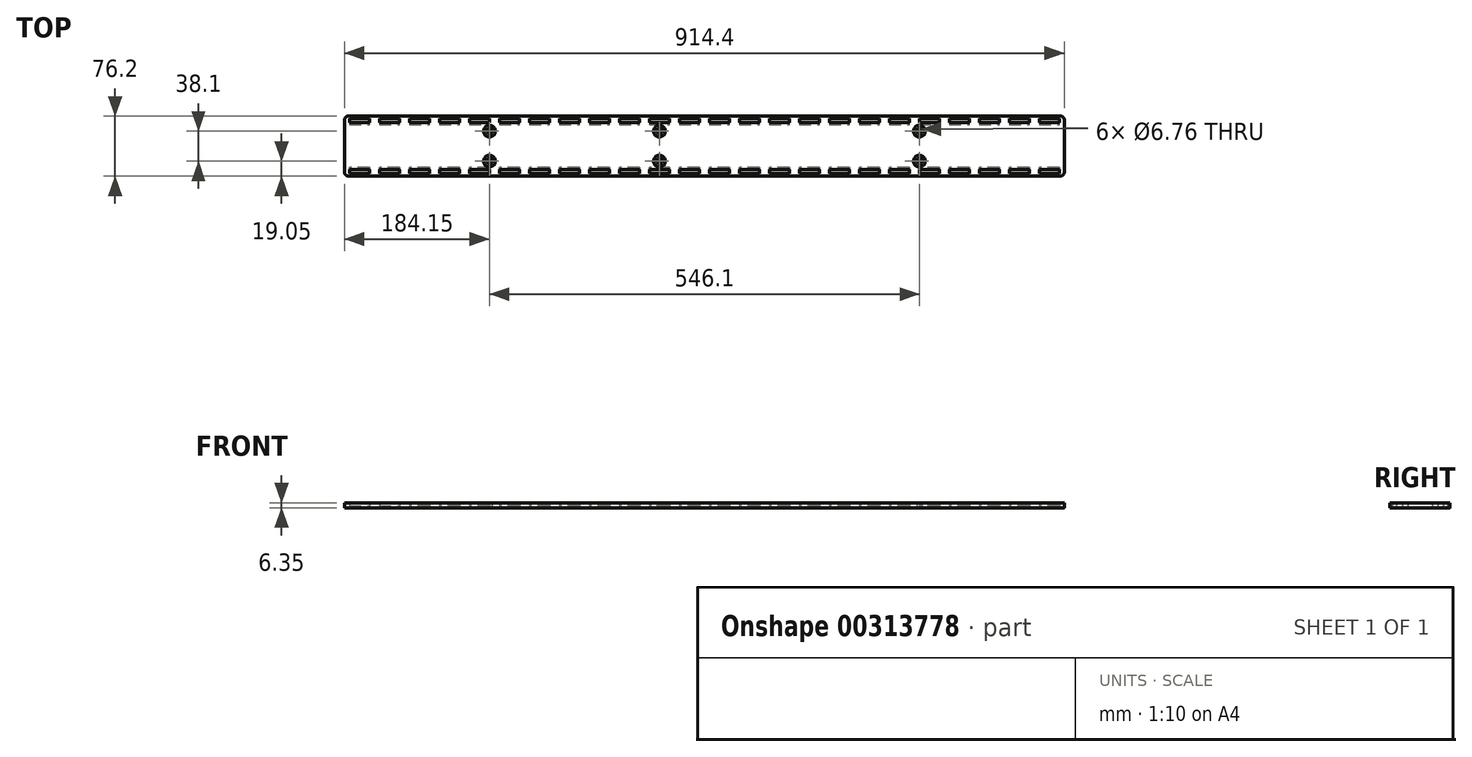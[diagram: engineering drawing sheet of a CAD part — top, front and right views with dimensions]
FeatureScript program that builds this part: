
annotation { "Feature Type Name" : "Feature", "Feature Type Description" : "" }
export const myFeature = defineFeature(function(context is Context, id is Id, definition is map)
    precondition{}
    {
        {
            var Q0;
            Q0=qCreatedBy(makeId("Top.planeOp"),FACE);
            var sketch = newSketch(context, id + "F0", { "sketchPlane" : qUnion([Q0])});
            skLineSegment(sketch, "E0.bottom", {"start": v(5.08, 0) * mm, "end": v(909.32, 0) * mm});
            skLineSegment(sketch, "E0.top", {"start": v(5.08, 76.2) * mm, "end": v(909.32, 76.2) * mm});
            skLineSegment(sketch, "E0.left", {"start": v(0, 5.08) * mm, "end": v(0, 71.12) * mm});
            skLineSegment(sketch, "E0.right", {"start": v(914.4, 5.08) * mm, "end": v(914.4, 71.12) * mm});
            skLineSegment(sketch, "E1", {"start": v(6.35, 73.03) * mm, "end": v(6.35, 67.94) * mm});
            skLineSegment(sketch, "E2", {"start": v(6.35, 67.94) * mm, "end": v(31.75, 67.95) * mm});
            skLineSegment(sketch, "E3", {"start": v(31.75, 67.95) * mm, "end": v(31.75, 73.03) * mm});
            skLineSegment(sketch, "E4", {"start": v(31.75, 73.03) * mm, "end": v(6.35, 73.03) * mm});
            skLineSegment(sketch, "E5.1.0.0", {"start": v(69.85, 73.03) * mm, "end": v(44.45, 73.03) * mm});
            skLineSegment(sketch, "E5.1.0.1", {"start": v(44.45, 73.03) * mm, "end": v(44.45, 67.94) * mm});
            skLineSegment(sketch, "E5.1.0.2", {"start": v(44.45, 67.94) * mm, "end": v(69.85, 67.95) * mm});
            skLineSegment(sketch, "E5.1.0.3", {"start": v(69.85, 67.95) * mm, "end": v(69.85, 73.03) * mm});
            skLineSegment(sketch, "E5.2.0.0", {"start": v(107.95, 73.03) * mm, "end": v(82.55, 73.03) * mm});
            skLineSegment(sketch, "E5.2.0.1", {"start": v(82.55, 73.03) * mm, "end": v(82.55, 67.94) * mm});
            skLineSegment(sketch, "E5.2.0.2", {"start": v(82.55, 67.94) * mm, "end": v(107.95, 67.95) * mm});
            skLineSegment(sketch, "E5.2.0.3", {"start": v(107.95, 67.95) * mm, "end": v(107.95, 73.03) * mm});
            skLineSegment(sketch, "E5.3.0.0", {"start": v(146.05, 73.03) * mm, "end": v(120.65, 73.03) * mm});
            skLineSegment(sketch, "E5.3.0.1", {"start": v(120.65, 73.03) * mm, "end": v(120.65, 67.94) * mm});
            skLineSegment(sketch, "E5.3.0.2", {"start": v(120.65, 67.94) * mm, "end": v(146.05, 67.95) * mm});
            skLineSegment(sketch, "E5.3.0.3", {"start": v(146.05, 67.95) * mm, "end": v(146.05, 73.03) * mm});
            skLineSegment(sketch, "E5.4.0.0", {"start": v(184.15, 73.03) * mm, "end": v(158.75, 73.03) * mm});
            skLineSegment(sketch, "E5.4.0.1", {"start": v(158.75, 73.03) * mm, "end": v(158.75, 67.94) * mm});
            skLineSegment(sketch, "E5.4.0.2", {"start": v(158.75, 67.94) * mm, "end": v(184.15, 67.95) * mm});
            skLineSegment(sketch, "E5.4.0.3", {"start": v(184.15, 67.95) * mm, "end": v(184.15, 73.03) * mm});
            skLineSegment(sketch, "E5.5.0.0", {"start": v(222.25, 73.03) * mm, "end": v(196.85, 73.03) * mm});
            skLineSegment(sketch, "E5.5.0.1", {"start": v(196.85, 73.03) * mm, "end": v(196.85, 67.94) * mm});
            skLineSegment(sketch, "E5.5.0.2", {"start": v(196.85, 67.94) * mm, "end": v(222.25, 67.95) * mm});
            skLineSegment(sketch, "E5.5.0.3", {"start": v(222.25, 67.95) * mm, "end": v(222.25, 73.03) * mm});
            skLineSegment(sketch, "E5.6.0.0", {"start": v(260.35, 73.03) * mm, "end": v(234.95, 73.03) * mm});
            skLineSegment(sketch, "E5.6.0.1", {"start": v(234.95, 73.03) * mm, "end": v(234.95, 67.94) * mm});
            skLineSegment(sketch, "E5.6.0.2", {"start": v(234.95, 67.94) * mm, "end": v(260.35, 67.95) * mm});
            skLineSegment(sketch, "E5.6.0.3", {"start": v(260.35, 67.95) * mm, "end": v(260.35, 73.03) * mm});
            skLineSegment(sketch, "E5.7.0.0", {"start": v(298.45, 73.03) * mm, "end": v(273.05, 73.03) * mm});
            skLineSegment(sketch, "E5.7.0.1", {"start": v(273.05, 73.03) * mm, "end": v(273.05, 67.94) * mm});
            skLineSegment(sketch, "E5.7.0.2", {"start": v(273.05, 67.94) * mm, "end": v(298.45, 67.95) * mm});
            skLineSegment(sketch, "E5.7.0.3", {"start": v(298.45, 67.95) * mm, "end": v(298.45, 73.03) * mm});
            skLineSegment(sketch, "E5.8.0.0", {"start": v(336.55, 73.03) * mm, "end": v(311.15, 73.03) * mm});
            skLineSegment(sketch, "E5.8.0.1", {"start": v(311.15, 73.03) * mm, "end": v(311.15, 67.94) * mm});
            skLineSegment(sketch, "E5.8.0.2", {"start": v(311.15, 67.94) * mm, "end": v(336.55, 67.95) * mm});
            skLineSegment(sketch, "E5.8.0.3", {"start": v(336.55, 67.95) * mm, "end": v(336.55, 73.03) * mm});
            skLineSegment(sketch, "E5.9.0.0", {"start": v(374.65, 73.03) * mm, "end": v(349.25, 73.03) * mm});
            skLineSegment(sketch, "E5.9.0.1", {"start": v(349.25, 73.03) * mm, "end": v(349.25, 67.94) * mm});
            skLineSegment(sketch, "E5.9.0.2", {"start": v(349.25, 67.94) * mm, "end": v(374.65, 67.95) * mm});
            skLineSegment(sketch, "E5.9.0.3", {"start": v(374.65, 67.95) * mm, "end": v(374.65, 73.03) * mm});
            skLineSegment(sketch, "E5.10.0.0", {"start": v(412.75, 73.03) * mm, "end": v(387.35, 73.03) * mm});
            skLineSegment(sketch, "E5.10.0.1", {"start": v(387.35, 73.03) * mm, "end": v(387.35, 67.94) * mm});
            skLineSegment(sketch, "E5.10.0.2", {"start": v(387.35, 67.94) * mm, "end": v(412.75, 67.95) * mm});
            skLineSegment(sketch, "E5.10.0.3", {"start": v(412.75, 67.95) * mm, "end": v(412.75, 73.03) * mm});
            skLineSegment(sketch, "E5.11.0.0", {"start": v(450.85, 73.03) * mm, "end": v(425.45, 73.03) * mm});
            skLineSegment(sketch, "E5.11.0.1", {"start": v(425.45, 73.03) * mm, "end": v(425.45, 67.94) * mm});
            skLineSegment(sketch, "E5.11.0.2", {"start": v(425.45, 67.94) * mm, "end": v(450.85, 67.95) * mm});
            skLineSegment(sketch, "E5.11.0.3", {"start": v(450.85, 67.95) * mm, "end": v(450.85, 73.03) * mm});
            skLineSegment(sketch, "E5.12.0.0", {"start": v(488.95, 73.03) * mm, "end": v(463.55, 73.03) * mm});
            skLineSegment(sketch, "E5.12.0.1", {"start": v(463.55, 73.03) * mm, "end": v(463.55, 67.94) * mm});
            skLineSegment(sketch, "E5.12.0.2", {"start": v(463.55, 67.94) * mm, "end": v(488.95, 67.95) * mm});
            skLineSegment(sketch, "E5.12.0.3", {"start": v(488.95, 67.95) * mm, "end": v(488.95, 73.03) * mm});
            skLineSegment(sketch, "E5.13.0.0", {"start": v(527.05, 73.03) * mm, "end": v(501.65, 73.03) * mm});
            skLineSegment(sketch, "E5.13.0.1", {"start": v(501.65, 73.03) * mm, "end": v(501.65, 67.94) * mm});
            skLineSegment(sketch, "E5.13.0.2", {"start": v(501.65, 67.94) * mm, "end": v(527.05, 67.95) * mm});
            skLineSegment(sketch, "E5.13.0.3", {"start": v(527.05, 67.95) * mm, "end": v(527.05, 73.03) * mm});
            skLineSegment(sketch, "E5.14.0.0", {"start": v(565.15, 73.03) * mm, "end": v(539.75, 73.03) * mm});
            skLineSegment(sketch, "E5.14.0.1", {"start": v(539.75, 73.03) * mm, "end": v(539.75, 67.94) * mm});
            skLineSegment(sketch, "E5.14.0.2", {"start": v(539.75, 67.94) * mm, "end": v(565.15, 67.95) * mm});
            skLineSegment(sketch, "E5.14.0.3", {"start": v(565.15, 67.95) * mm, "end": v(565.15, 73.03) * mm});
            skLineSegment(sketch, "E5.15.0.0", {"start": v(603.25, 73.03) * mm, "end": v(577.85, 73.03) * mm});
            skLineSegment(sketch, "E5.15.0.1", {"start": v(577.85, 73.03) * mm, "end": v(577.85, 67.94) * mm});
            skLineSegment(sketch, "E5.15.0.2", {"start": v(577.85, 67.94) * mm, "end": v(603.25, 67.95) * mm});
            skLineSegment(sketch, "E5.15.0.3", {"start": v(603.25, 67.95) * mm, "end": v(603.25, 73.03) * mm});
            skLineSegment(sketch, "E5.16.0.0", {"start": v(641.35, 73.03) * mm, "end": v(615.95, 73.03) * mm});
            skLineSegment(sketch, "E5.16.0.1", {"start": v(615.95, 73.03) * mm, "end": v(615.95, 67.94) * mm});
            skLineSegment(sketch, "E5.16.0.2", {"start": v(615.95, 67.94) * mm, "end": v(641.35, 67.95) * mm});
            skLineSegment(sketch, "E5.16.0.3", {"start": v(641.35, 67.95) * mm, "end": v(641.35, 73.03) * mm});
            skLineSegment(sketch, "E5.17.0.0", {"start": v(679.45, 73.03) * mm, "end": v(654.05, 73.03) * mm});
            skLineSegment(sketch, "E5.17.0.1", {"start": v(654.05, 73.03) * mm, "end": v(654.05, 67.94) * mm});
            skLineSegment(sketch, "E5.17.0.2", {"start": v(654.05, 67.94) * mm, "end": v(679.45, 67.95) * mm});
            skLineSegment(sketch, "E5.17.0.3", {"start": v(679.45, 67.95) * mm, "end": v(679.45, 73.03) * mm});
            skLineSegment(sketch, "E5.18.0.0", {"start": v(717.55, 73.03) * mm, "end": v(692.15, 73.03) * mm});
            skLineSegment(sketch, "E5.18.0.1", {"start": v(692.15, 73.03) * mm, "end": v(692.15, 67.94) * mm});
            skLineSegment(sketch, "E5.18.0.2", {"start": v(692.15, 67.94) * mm, "end": v(717.55, 67.95) * mm});
            skLineSegment(sketch, "E5.18.0.3", {"start": v(717.55, 67.95) * mm, "end": v(717.55, 73.03) * mm});
            skLineSegment(sketch, "E5.19.0.0", {"start": v(755.65, 73.03) * mm, "end": v(730.25, 73.03) * mm});
            skLineSegment(sketch, "E5.19.0.1", {"start": v(730.25, 73.03) * mm, "end": v(730.25, 67.94) * mm});
            skLineSegment(sketch, "E5.19.0.2", {"start": v(730.25, 67.94) * mm, "end": v(755.65, 67.95) * mm});
            skLineSegment(sketch, "E5.19.0.3", {"start": v(755.65, 67.95) * mm, "end": v(755.65, 73.03) * mm});
            skLineSegment(sketch, "E5.20.0.0", {"start": v(793.75, 73.03) * mm, "end": v(768.35, 73.03) * mm});
            skLineSegment(sketch, "E5.20.0.1", {"start": v(768.35, 73.03) * mm, "end": v(768.35, 67.94) * mm});
            skLineSegment(sketch, "E5.20.0.2", {"start": v(768.35, 67.94) * mm, "end": v(793.75, 67.95) * mm});
            skLineSegment(sketch, "E5.20.0.3", {"start": v(793.75, 67.95) * mm, "end": v(793.75, 73.03) * mm});
            skLineSegment(sketch, "E5.21.0.0", {"start": v(831.85, 73.03) * mm, "end": v(806.45, 73.03) * mm});
            skLineSegment(sketch, "E5.21.0.1", {"start": v(806.45, 73.03) * mm, "end": v(806.45, 67.94) * mm});
            skLineSegment(sketch, "E5.21.0.2", {"start": v(806.45, 67.94) * mm, "end": v(831.85, 67.95) * mm});
            skLineSegment(sketch, "E5.21.0.3", {"start": v(831.85, 67.95) * mm, "end": v(831.85, 73.03) * mm});
            skLineSegment(sketch, "E5.22.0.0", {"start": v(869.95, 73.03) * mm, "end": v(844.55, 73.03) * mm});
            skLineSegment(sketch, "E5.22.0.1", {"start": v(844.55, 73.03) * mm, "end": v(844.55, 67.94) * mm});
            skLineSegment(sketch, "E5.22.0.2", {"start": v(844.55, 67.94) * mm, "end": v(869.95, 67.95) * mm});
            skLineSegment(sketch, "E5.22.0.3", {"start": v(869.95, 67.95) * mm, "end": v(869.95, 73.03) * mm});
            skLineSegment(sketch, "E5.23.0.0", {"start": v(908.05, 73.03) * mm, "end": v(882.65, 73.03) * mm});
            skLineSegment(sketch, "E5.23.0.1", {"start": v(882.65, 73.03) * mm, "end": v(882.65, 67.94) * mm});
            skLineSegment(sketch, "E5.23.0.2", {"start": v(882.65, 67.94) * mm, "end": v(908.05, 67.95) * mm});
            skLineSegment(sketch, "E5.23.0.3", {"start": v(908.05, 67.95) * mm, "end": v(908.05, 73.03) * mm});
            skLineSegment(sketch, "E6.MirrorCS", {"start": v(488.95, 8.25) * mm, "end": v(488.95, 3.17) * mm});
            skLineSegment(sketch, "E7.MirrorCS", {"start": v(336.55, 8.25) * mm, "end": v(336.55, 3.17) * mm});
            skLineSegment(sketch, "E8.MirrorCS", {"start": v(184.15, 8.25) * mm, "end": v(184.15, 3.17) * mm});
            skLineSegment(sketch, "E9.MirrorCS", {"start": v(793.75, 8.25) * mm, "end": v(793.75, 3.17) * mm});
            skLineSegment(sketch, "E10.MirrorCS", {"start": v(641.35, 8.25) * mm, "end": v(641.35, 3.17) * mm});
            skLineSegment(sketch, "E11.MirrorCS", {"start": v(120.65, 3.17) * mm, "end": v(120.65, 8.26) * mm});
            skLineSegment(sketch, "E12.MirrorCS", {"start": v(730.25, 3.17) * mm, "end": v(730.25, 8.26) * mm});
            skLineSegment(sketch, "E13.MirrorCS", {"start": v(577.85, 3.17) * mm, "end": v(577.85, 8.26) * mm});
            skLineSegment(sketch, "E14.MirrorCS", {"start": v(425.45, 3.17) * mm, "end": v(425.45, 8.26) * mm});
            skLineSegment(sketch, "E15.MirrorCS", {"start": v(273.05, 3.17) * mm, "end": v(273.05, 8.26) * mm});
            skLineSegment(sketch, "E16.MirrorCS", {"start": v(882.65, 3.17) * mm, "end": v(882.65, 8.26) * mm});
            skLineSegment(sketch, "E17.MirrorCS", {"start": v(501.65, 3.17) * mm, "end": v(501.65, 8.26) * mm});
            skLineSegment(sketch, "E18.MirrorCS", {"start": v(349.25, 3.17) * mm, "end": v(349.25, 8.26) * mm});
            skLineSegment(sketch, "E19.MirrorCS", {"start": v(196.85, 3.17) * mm, "end": v(196.85, 8.26) * mm});
            skLineSegment(sketch, "E20.MirrorCS", {"start": v(806.45, 3.17) * mm, "end": v(806.45, 8.26) * mm});
            skLineSegment(sketch, "E21.MirrorCS", {"start": v(654.05, 3.17) * mm, "end": v(654.05, 8.26) * mm});
            skLineSegment(sketch, "E22.MirrorCS", {"start": v(679.45, 8.25) * mm, "end": v(679.45, 3.17) * mm});
            skLineSegment(sketch, "E23.MirrorCS", {"start": v(527.05, 8.25) * mm, "end": v(527.05, 3.17) * mm});
            skLineSegment(sketch, "E24.MirrorCS", {"start": v(374.65, 8.25) * mm, "end": v(374.65, 3.17) * mm});
            skLineSegment(sketch, "E25.MirrorCS", {"start": v(222.25, 8.25) * mm, "end": v(222.25, 3.17) * mm});
            skLineSegment(sketch, "E26.MirrorCS", {"start": v(831.85, 8.25) * mm, "end": v(831.85, 3.17) * mm});
            skLineSegment(sketch, "E27.MirrorCS", {"start": v(146.05, 8.25) * mm, "end": v(146.05, 3.17) * mm});
            skLineSegment(sketch, "E28.MirrorCS", {"start": v(755.65, 8.25) * mm, "end": v(755.65, 3.17) * mm});
            skLineSegment(sketch, "E29.MirrorCS", {"start": v(603.25, 8.25) * mm, "end": v(603.25, 3.17) * mm});
            skLineSegment(sketch, "E30.MirrorCS", {"start": v(450.85, 8.25) * mm, "end": v(450.85, 3.17) * mm});
            skLineSegment(sketch, "E31.MirrorCS", {"start": v(298.45, 8.25) * mm, "end": v(298.45, 3.17) * mm});
            skLineSegment(sketch, "E32.MirrorCS", {"start": v(908.05, 8.25) * mm, "end": v(908.05, 3.17) * mm});
            skLineSegment(sketch, "E33.MirrorCS", {"start": v(69.85, 8.25) * mm, "end": v(69.85, 3.17) * mm});
            skLineSegment(sketch, "E34.MirrorCS", {"start": v(6.35, 3.17) * mm, "end": v(6.35, 8.26) * mm});
            skLineSegment(sketch, "E35.MirrorCS", {"start": v(31.75, 8.25) * mm, "end": v(31.75, 3.17) * mm});
            skLineSegment(sketch, "E36.MirrorCS", {"start": v(44.45, 3.17) * mm, "end": v(44.45, 8.26) * mm});
            skLineSegment(sketch, "E37.MirrorCS", {"start": v(844.55, 3.17) * mm, "end": v(844.55, 8.26) * mm});
            skLineSegment(sketch, "E38.MirrorCS", {"start": v(82.55, 3.17) * mm, "end": v(82.55, 8.26) * mm});
            skLineSegment(sketch, "E39.MirrorCS", {"start": v(692.15, 3.17) * mm, "end": v(692.15, 8.26) * mm});
            skLineSegment(sketch, "E40.MirrorCS", {"start": v(539.75, 3.17) * mm, "end": v(539.75, 8.26) * mm});
            skLineSegment(sketch, "E41.MirrorCS", {"start": v(234.95, 3.17) * mm, "end": v(234.95, 8.26) * mm});
            skLineSegment(sketch, "E42.MirrorCS", {"start": v(387.35, 3.17) * mm, "end": v(387.35, 8.26) * mm});
            skLineSegment(sketch, "E43.MirrorCS", {"start": v(463.55, 3.17) * mm, "end": v(463.55, 8.26) * mm});
            skLineSegment(sketch, "E44.MirrorCS", {"start": v(158.75, 3.17) * mm, "end": v(158.75, 8.26) * mm});
            skLineSegment(sketch, "E45.MirrorCS", {"start": v(768.35, 3.17) * mm, "end": v(768.35, 8.26) * mm});
            skLineSegment(sketch, "E46.MirrorCS", {"start": v(615.95, 3.17) * mm, "end": v(615.95, 8.26) * mm});
            skLineSegment(sketch, "E47.MirrorCS", {"start": v(311.15, 3.17) * mm, "end": v(311.15, 8.26) * mm});
            skLineSegment(sketch, "E48.MirrorCS", {"start": v(869.95, 8.25) * mm, "end": v(869.95, 3.17) * mm});
            skLineSegment(sketch, "E49.MirrorCS", {"start": v(107.95, 8.25) * mm, "end": v(107.95, 3.17) * mm});
            skLineSegment(sketch, "E50.MirrorCS", {"start": v(717.55, 8.25) * mm, "end": v(717.55, 3.17) * mm});
            skLineSegment(sketch, "E51.MirrorCS", {"start": v(565.15, 8.25) * mm, "end": v(565.15, 3.17) * mm});
            skLineSegment(sketch, "E52.MirrorCS", {"start": v(412.75, 8.25) * mm, "end": v(412.75, 3.17) * mm});
            skLineSegment(sketch, "E53.MirrorCS", {"start": v(260.35, 8.25) * mm, "end": v(260.35, 3.17) * mm});
            skLineSegment(sketch, "E54.MirrorCS", {"start": v(31.75, 3.17) * mm, "end": v(6.35, 3.17) * mm});
            skLineSegment(sketch, "E55.MirrorCS", {"start": v(146.05, 3.17) * mm, "end": v(120.65, 3.17) * mm});
            skLineSegment(sketch, "E56.MirrorCS", {"start": v(755.65, 3.17) * mm, "end": v(730.25, 3.17) * mm});
            skLineSegment(sketch, "E57.MirrorCS", {"start": v(603.25, 3.17) * mm, "end": v(577.85, 3.17) * mm});
            skLineSegment(sketch, "E58.MirrorCS", {"start": v(450.85, 3.17) * mm, "end": v(425.45, 3.17) * mm});
            skLineSegment(sketch, "E59.MirrorCS", {"start": v(298.45, 3.17) * mm, "end": v(273.05, 3.17) * mm});
            skLineSegment(sketch, "E60.MirrorCS", {"start": v(908.05, 3.17) * mm, "end": v(882.65, 3.17) * mm});
            skLineSegment(sketch, "E61.MirrorCS", {"start": v(527.05, 3.17) * mm, "end": v(501.65, 3.17) * mm});
            skLineSegment(sketch, "E62.MirrorCS", {"start": v(374.65, 3.17) * mm, "end": v(349.25, 3.17) * mm});
            skLineSegment(sketch, "E63.MirrorCS", {"start": v(222.25, 3.17) * mm, "end": v(196.85, 3.17) * mm});
            skLineSegment(sketch, "E64.MirrorCS", {"start": v(831.85, 3.17) * mm, "end": v(806.45, 3.17) * mm});
            skLineSegment(sketch, "E65.MirrorCS", {"start": v(679.45, 3.17) * mm, "end": v(654.05, 3.17) * mm});
            skLineSegment(sketch, "E66.MirrorCS", {"start": v(654.05, 8.26) * mm, "end": v(679.45, 8.26) * mm});
            skLineSegment(sketch, "E67.MirrorCS", {"start": v(501.65, 8.26) * mm, "end": v(527.05, 8.26) * mm});
            skLineSegment(sketch, "E68.MirrorCS", {"start": v(349.25, 8.26) * mm, "end": v(374.65, 8.26) * mm});
            skLineSegment(sketch, "E69.MirrorCS", {"start": v(196.85, 8.26) * mm, "end": v(222.25, 8.26) * mm});
            skLineSegment(sketch, "E70.MirrorCS", {"start": v(806.45, 8.26) * mm, "end": v(831.85, 8.26) * mm});
            skLineSegment(sketch, "E71.MirrorCS", {"start": v(120.65, 8.26) * mm, "end": v(146.05, 8.26) * mm});
            skLineSegment(sketch, "E72.MirrorCS", {"start": v(730.25, 8.26) * mm, "end": v(755.65, 8.26) * mm});
            skLineSegment(sketch, "E73.MirrorCS", {"start": v(577.85, 8.26) * mm, "end": v(603.25, 8.26) * mm});
            skLineSegment(sketch, "E74.MirrorCS", {"start": v(425.45, 8.26) * mm, "end": v(450.85, 8.26) * mm});
            skLineSegment(sketch, "E75.MirrorCS", {"start": v(273.05, 8.26) * mm, "end": v(298.45, 8.26) * mm});
            skLineSegment(sketch, "E76.MirrorCS", {"start": v(882.65, 8.26) * mm, "end": v(908.05, 8.26) * mm});
            skLineSegment(sketch, "E77.MirrorCS", {"start": v(717.55, 3.17) * mm, "end": v(692.15, 3.17) * mm});
            skLineSegment(sketch, "E78.MirrorCS", {"start": v(565.15, 3.17) * mm, "end": v(539.75, 3.17) * mm});
            skLineSegment(sketch, "E79.MirrorCS", {"start": v(412.75, 3.17) * mm, "end": v(387.35, 3.17) * mm});
            skLineSegment(sketch, "E80.MirrorCS", {"start": v(260.35, 3.17) * mm, "end": v(234.95, 3.17) * mm});
            skLineSegment(sketch, "E81.MirrorCS", {"start": v(44.45, 8.26) * mm, "end": v(69.85, 8.26) * mm});
            skLineSegment(sketch, "E82.MirrorCS", {"start": v(869.95, 3.17) * mm, "end": v(844.55, 3.17) * mm});
            skLineSegment(sketch, "E83.MirrorCS", {"start": v(107.95, 3.17) * mm, "end": v(82.55, 3.17) * mm});
            skLineSegment(sketch, "E84.MirrorCS", {"start": v(6.35, 8.26) * mm, "end": v(31.75, 8.26) * mm});
            skLineSegment(sketch, "E85.MirrorCS", {"start": v(69.85, 3.17) * mm, "end": v(44.45, 3.17) * mm});
            skLineSegment(sketch, "E86.MirrorCS", {"start": v(336.55, 3.17) * mm, "end": v(311.15, 3.17) * mm});
            skLineSegment(sketch, "E87.MirrorCS", {"start": v(488.95, 3.17) * mm, "end": v(463.55, 3.17) * mm});
            skLineSegment(sketch, "E88.MirrorCS", {"start": v(184.15, 3.17) * mm, "end": v(158.75, 3.17) * mm});
            skLineSegment(sketch, "E89.MirrorCS", {"start": v(793.75, 3.17) * mm, "end": v(768.35, 3.17) * mm});
            skLineSegment(sketch, "E90.MirrorCS", {"start": v(641.35, 3.17) * mm, "end": v(615.95, 3.17) * mm});
            skLineSegment(sketch, "E91.MirrorCS", {"start": v(844.55, 8.26) * mm, "end": v(869.95, 8.26) * mm});
            skLineSegment(sketch, "E92.MirrorCS", {"start": v(158.75, 8.26) * mm, "end": v(184.15, 8.26) * mm});
            skLineSegment(sketch, "E93.MirrorCS", {"start": v(82.55, 8.26) * mm, "end": v(107.95, 8.26) * mm});
            skLineSegment(sketch, "E94.MirrorCS", {"start": v(539.75, 8.26) * mm, "end": v(565.15, 8.26) * mm});
            skLineSegment(sketch, "E95.MirrorCS", {"start": v(692.15, 8.26) * mm, "end": v(717.55, 8.26) * mm});
            skLineSegment(sketch, "E96.MirrorCS", {"start": v(234.95, 8.26) * mm, "end": v(260.35, 8.26) * mm});
            skLineSegment(sketch, "E97.MirrorCS", {"start": v(387.35, 8.26) * mm, "end": v(412.75, 8.26) * mm});
            skLineSegment(sketch, "E98.MirrorCS", {"start": v(615.95, 8.26) * mm, "end": v(641.35, 8.26) * mm});
            skLineSegment(sketch, "E99.MirrorCS", {"start": v(463.55, 8.26) * mm, "end": v(488.95, 8.26) * mm});
            skLineSegment(sketch, "E100.MirrorCS", {"start": v(311.15, 8.26) * mm, "end": v(336.55, 8.26) * mm});
            skLineSegment(sketch, "E101.MirrorCS", {"start": v(768.35, 8.26) * mm, "end": v(793.75, 8.26) * mm});
            skPoint(sketch, "E102.startSnap0", {"position": v(0, 38.1) * mm});
            skCircle(sketch, "E103", {"center": v(184.15, 57.15) * mm, "radius": 3.38 * mm});
            skCircle(sketch, "E104", {"center": v(400.05, 57.15) * mm, "radius": 3.38 * mm});
            skCircle(sketch, "E105", {"center": v(730.25, 57.15) * mm, "radius": 3.38 * mm});
            skCircle(sketch, "E106.MirrorC", {"center": v(730.25, 19.05) * mm, "radius": 3.38 * mm});
            skCircle(sketch, "E107.MirrorC", {"center": v(400.05, 19.05) * mm, "radius": 3.38 * mm});
            skCircle(sketch, "E108.MirrorC", {"center": v(184.15, 19.05) * mm, "radius": 3.38 * mm});
            skArc(sketch, "E109", {"start": v(5.08, 76.2) * mm, "mid": v(1.49, 74.71) * mm, "end": v(0, 71.12) * mm});
            skPoint(sketch, "E110.orphan", {"position": v(0, 76.2) * mm});
            skArc(sketch, "E111", {"start": v(0, 5.08) * mm, "mid": v(1.49, 1.49) * mm, "end": v(5.08, 0) * mm});
            skPoint(sketch, "E112.orphan", {"position": v(0, 0) * mm});
            skArc(sketch, "E113", {"start": v(909.32, 0) * mm, "mid": v(912.91, 1.49) * mm, "end": v(914.4, 5.08) * mm});
            skArc(sketch, "E114", {"start": v(914.4, 71.12) * mm, "mid": v(912.91, 74.71) * mm, "end": v(909.32, 76.2) * mm});
            skSolve(sketch);
        }
        {
            var Q0;
            Q0 = qSketchRegion(id + "F0", true);
            extrude(context, id + "F1", {"entities" : qUnion([Q0]), "depth" : 6.35 * mm});
        }
        {
            var Q0;
            Q0=makeQuery(id+"F1.opExtrude","CAP_EDGE",EDGE,{"disambiguationData":[OSD([sQuery(id+"F0.wireOp",EDGE,"E5.14.0.2")])],"isStart":true});
            var Q1;
            Q1=makeQuery(id+"F1.opExtrude","CAP_EDGE",EDGE,{"disambiguationData":[OSD([sQuery(id+"F0.wireOp",EDGE,"E5.13.0.2")])],"isStart":true});
            var Q2;
            Q2=makeQuery(id+"F1.opExtrude","CAP_EDGE",EDGE,{"disambiguationData":[OSD([sQuery(id+"F0.wireOp",EDGE,"E5.12.0.2")])],"isStart":true});
            var Q3;
            Q3=makeQuery(id+"F1.opExtrude","CAP_EDGE",EDGE,{"disambiguationData":[OSD([sQuery(id+"F0.wireOp",EDGE,"E5.11.0.2")])],"isStart":true});
            var Q4;
            Q4=makeQuery(id+"F1.opExtrude","CAP_EDGE",EDGE,{"disambiguationData":[OSD([sQuery(id+"F0.wireOp",EDGE,"E5.10.0.2")])],"isStart":true});
            var Q5;
            Q5=makeQuery(id+"F1.opExtrude","CAP_EDGE",EDGE,{"disambiguationData":[OSD([sQuery(id+"F0.wireOp",EDGE,"E5.9.0.2")])],"isStart":true});
            var Q6;
            Q6=makeQuery(id+"F1.opExtrude","CAP_EDGE",EDGE,{"disambiguationData":[OSD([sQuery(id+"F0.wireOp",EDGE,"E5.8.0.2")])],"isStart":true});
            var Q7;
            Q7=makeQuery(id+"F1.opExtrude","CAP_EDGE",EDGE,{"disambiguationData":[OSD([sQuery(id+"F0.wireOp",EDGE,"E5.7.0.2")])],"isStart":true});
            var Q8;
            Q8=makeQuery(id+"F1.opExtrude","CAP_EDGE",EDGE,{"disambiguationData":[OSD([sQuery(id+"F0.wireOp",EDGE,"E5.6.0.2")])],"isStart":true});
            var Q9;
            Q9=makeQuery(id+"F1.opExtrude","CAP_EDGE",EDGE,{"disambiguationData":[OSD([sQuery(id+"F0.wireOp",EDGE,"E5.5.0.2")])],"isStart":true});
            var Q10;
            Q10=makeQuery(id+"F1.opExtrude","CAP_EDGE",EDGE,{"disambiguationData":[OSD([sQuery(id+"F0.wireOp",EDGE,"E5.4.0.2")])],"isStart":true});
            var Q11;
            Q11=makeQuery(id+"F1.opExtrude","CAP_EDGE",EDGE,{"disambiguationData":[OSD([sQuery(id+"F0.wireOp",EDGE,"E5.3.0.2")])],"isStart":true});
            var Q12;
            Q12=makeQuery(id+"F1.opExtrude","CAP_EDGE",EDGE,{"disambiguationData":[OSD([sQuery(id+"F0.wireOp",EDGE,"E5.2.0.2")])],"isStart":true});
            var Q13;
            Q13=makeQuery(id+"F1.opExtrude","CAP_EDGE",EDGE,{"disambiguationData":[OSD([sQuery(id+"F0.wireOp",EDGE,"E5.1.0.2")])],"isStart":true});
            var Q14;
            Q14=makeQuery(id+"F1.opExtrude","CAP_EDGE",EDGE,{"disambiguationData":[OSD([sQuery(id+"F0.wireOp",EDGE,"E2")])],"isStart":true});
            var Q15;
            Q15=makeQuery(id+"F1.opExtrude","CAP_EDGE",EDGE,{"disambiguationData":[OSD([sQuery(id+"F0.wireOp",EDGE,"E84.MirrorCS")])],"isStart":true});
            var Q16;
            Q16=makeQuery(id+"F1.opExtrude","CAP_EDGE",EDGE,{"disambiguationData":[OSD([sQuery(id+"F0.wireOp",EDGE,"E81.MirrorCS")])],"isStart":true});
            var Q17;
            Q17=makeQuery(id+"F1.opExtrude","CAP_EDGE",EDGE,{"disambiguationData":[OSD([sQuery(id+"F0.wireOp",EDGE,"E93.MirrorCS")])],"isStart":true});
            var Q18;
            Q18=makeQuery(id+"F1.opExtrude","CAP_EDGE",EDGE,{"disambiguationData":[OSD([sQuery(id+"F0.wireOp",EDGE,"E71.MirrorCS")])],"isStart":true});
            var Q19;
            Q19=makeQuery(id+"F1.opExtrude","CAP_EDGE",EDGE,{"disambiguationData":[OSD([sQuery(id+"F0.wireOp",EDGE,"E92.MirrorCS")])],"isStart":true});
            var Q20;
            Q20=makeQuery(id+"F1.opExtrude","CAP_EDGE",EDGE,{"disambiguationData":[OSD([sQuery(id+"F0.wireOp",EDGE,"E69.MirrorCS")])],"isStart":true});
            var Q21;
            Q21=makeQuery(id+"F1.opExtrude","CAP_EDGE",EDGE,{"disambiguationData":[OSD([sQuery(id+"F0.wireOp",EDGE,"E96.MirrorCS")])],"isStart":true});
            var Q22;
            Q22=makeQuery(id+"F1.opExtrude","CAP_EDGE",EDGE,{"disambiguationData":[OSD([sQuery(id+"F0.wireOp",EDGE,"E75.MirrorCS")])],"isStart":true});
            var Q23;
            Q23=makeQuery(id+"F1.opExtrude","CAP_EDGE",EDGE,{"disambiguationData":[OSD([sQuery(id+"F0.wireOp",EDGE,"E100.MirrorCS")])],"isStart":true});
            var Q24;
            Q24=makeQuery(id+"F1.opExtrude","CAP_EDGE",EDGE,{"disambiguationData":[OSD([sQuery(id+"F0.wireOp",EDGE,"E68.MirrorCS")])],"isStart":true});
            var Q25;
            Q25=makeQuery(id+"F1.opExtrude","CAP_EDGE",EDGE,{"disambiguationData":[OSD([sQuery(id+"F0.wireOp",EDGE,"E97.MirrorCS")])],"isStart":true});
            var Q26;
            Q26=makeQuery(id+"F1.opExtrude","CAP_EDGE",EDGE,{"disambiguationData":[OSD([sQuery(id+"F0.wireOp",EDGE,"E74.MirrorCS")])],"isStart":true});
            var Q27;
            Q27=makeQuery(id+"F1.opExtrude","CAP_EDGE",EDGE,{"disambiguationData":[OSD([sQuery(id+"F0.wireOp",EDGE,"E99.MirrorCS")])],"isStart":true});
            var Q28;
            Q28=makeQuery(id+"F1.opExtrude","CAP_EDGE",EDGE,{"disambiguationData":[OSD([sQuery(id+"F0.wireOp",EDGE,"E94.MirrorCS")])],"isStart":true});
            var Q29;
            Q29=makeQuery(id+"F1.opExtrude","CAP_EDGE",EDGE,{"disambiguationData":[OSD([sQuery(id+"F0.wireOp",EDGE,"E73.MirrorCS")])],"isStart":true});
            var Q30;
            Q30=makeQuery(id+"F1.opExtrude","CAP_EDGE",EDGE,{"disambiguationData":[OSD([sQuery(id+"F0.wireOp",EDGE,"E98.MirrorCS")])],"isStart":true});
            var Q31;
            Q31=makeQuery(id+"F1.opExtrude","CAP_EDGE",EDGE,{"disambiguationData":[OSD([sQuery(id+"F0.wireOp",EDGE,"E66.MirrorCS")])],"isStart":true});
            var Q32;
            Q32=makeQuery(id+"F1.opExtrude","CAP_EDGE",EDGE,{"disambiguationData":[OSD([sQuery(id+"F0.wireOp",EDGE,"E95.MirrorCS")])],"isStart":true});
            var Q33;
            Q33=makeQuery(id+"F1.opExtrude","CAP_EDGE",EDGE,{"disambiguationData":[OSD([sQuery(id+"F0.wireOp",EDGE,"E72.MirrorCS")])],"isStart":true});
            var Q34;
            Q34=makeQuery(id+"F1.opExtrude","CAP_EDGE",EDGE,{"disambiguationData":[OSD([sQuery(id+"F0.wireOp",EDGE,"E101.MirrorCS")])],"isStart":true});
            var Q35;
            Q35=makeQuery(id+"F1.opExtrude","CAP_EDGE",EDGE,{"disambiguationData":[OSD([sQuery(id+"F0.wireOp",EDGE,"E70.MirrorCS")])],"isStart":true});
            var Q36;
            Q36=makeQuery(id+"F1.opExtrude","CAP_EDGE",EDGE,{"disambiguationData":[OSD([sQuery(id+"F0.wireOp",EDGE,"E91.MirrorCS")])],"isStart":true});
            var Q37;
            Q37=makeQuery(id+"F1.opExtrude","CAP_EDGE",EDGE,{"disambiguationData":[OSD([sQuery(id+"F0.wireOp",EDGE,"E67.MirrorCS")])],"isStart":true});
            var Q38;
            Q38=makeQuery(id+"F1.opExtrude","CAP_EDGE",EDGE,{"disambiguationData":[OSD([sQuery(id+"F0.wireOp",EDGE,"E5.15.0.2")])],"isStart":true});
            var Q39;
            Q39=makeQuery(id+"F1.opExtrude","CAP_EDGE",EDGE,{"disambiguationData":[OSD([sQuery(id+"F0.wireOp",EDGE,"E5.16.0.2")])],"isStart":true});
            var Q40;
            Q40=makeQuery(id+"F1.opExtrude","CAP_EDGE",EDGE,{"disambiguationData":[OSD([sQuery(id+"F0.wireOp",EDGE,"E5.17.0.2")])],"isStart":true});
            var Q41;
            Q41=makeQuery(id+"F1.opExtrude","CAP_EDGE",EDGE,{"disambiguationData":[OSD([sQuery(id+"F0.wireOp",EDGE,"E5.18.0.2")])],"isStart":true});
            var Q42;
            Q42=makeQuery(id+"F1.opExtrude","CAP_EDGE",EDGE,{"disambiguationData":[OSD([sQuery(id+"F0.wireOp",EDGE,"E5.19.0.2")])],"isStart":true});
            var Q43;
            Q43=makeQuery(id+"F1.opExtrude","CAP_EDGE",EDGE,{"disambiguationData":[OSD([sQuery(id+"F0.wireOp",EDGE,"E5.20.0.2")])],"isStart":true});
            var Q44;
            Q44=makeQuery(id+"F1.opExtrude","CAP_EDGE",EDGE,{"disambiguationData":[OSD([sQuery(id+"F0.wireOp",EDGE,"E5.21.0.2")])],"isStart":true});
            var Q45;
            Q45=makeQuery(id+"F1.opExtrude","CAP_EDGE",EDGE,{"disambiguationData":[OSD([sQuery(id+"F0.wireOp",EDGE,"E5.22.0.2")])],"isStart":true});
            var Q46;
            Q46=makeQuery(id+"F1.opExtrude","CAP_EDGE",EDGE,{"disambiguationData":[OSD([sQuery(id+"F0.wireOp",EDGE,"E5.23.0.2")])],"isStart":true});
            var Q47;
            Q47=makeQuery(id+"F1.opExtrude","CAP_EDGE",EDGE,{"disambiguationData":[OSD([sQuery(id+"F0.wireOp",EDGE,"E76.MirrorCS")])],"isStart":true});
            chamfer(context, id + "F2", {"entities" : qUnion([Q0, Q1, Q2, Q3, Q4, Q5, Q6, Q7, Q8, Q9, Q10, Q11, Q12, Q13, Q14, Q15, Q16, Q17, Q18, Q19, Q20, Q21, Q22, Q23, Q24, Q25, Q26, Q27, Q28, Q29, Q30, Q31, Q32, Q33, Q34, Q35, Q36, Q37, Q38, Q39, Q40, Q41, Q42, Q43, Q44, Q45, Q46, Q47]), "width" : 2.54 * mm, "tangentPropagation" : true});
        }
        {
            var Q0;
            Q0=makeQuery(id+"F1.opExtrude","CAP_EDGE",EDGE,{"disambiguationData":[OSD([sQuery(id+"F0.wireOp",EDGE,"E107.MirrorC")])],"isStart":false});
            var Q1;
            Q1=makeQuery(id+"F1.opExtrude","CAP_EDGE",EDGE,{"disambiguationData":[OSD([sQuery(id+"F0.wireOp",EDGE,"E104")])],"isStart":false});
            var Q2;
            Q2=makeQuery(id+"F1.opExtrude","CAP_EDGE",EDGE,{"disambiguationData":[OSD([sQuery(id+"F0.wireOp",EDGE,"E108.MirrorC")])],"isStart":false});
            var Q3;
            Q3=makeQuery(id+"F1.opExtrude","CAP_EDGE",EDGE,{"disambiguationData":[OSD([sQuery(id+"F0.wireOp",EDGE,"E103")])],"isStart":false});
            var Q4;
            Q4=makeQuery(id+"F1.opExtrude","CAP_EDGE",EDGE,{"disambiguationData":[OSD([sQuery(id+"F0.wireOp",EDGE,"E106.MirrorC")])],"isStart":false});
            var Q5;
            Q5=makeQuery(id+"F1.opExtrude","CAP_EDGE",EDGE,{"disambiguationData":[OSD([sQuery(id+"F0.wireOp",EDGE,"E105")])],"isStart":false});
            chamfer(context, id + "F3", {"entities" : qUnion([Q0, Q1, Q2, Q3, Q4, Q5]), "chamferType" : ChamferType.TWO_OFFSETS, "width1" : ((.531 - .266) / 2) * mm, "oppositeDirection" : false, "width2" : 4.1 * mm, "tangentPropagation" : true});
        }
    });
